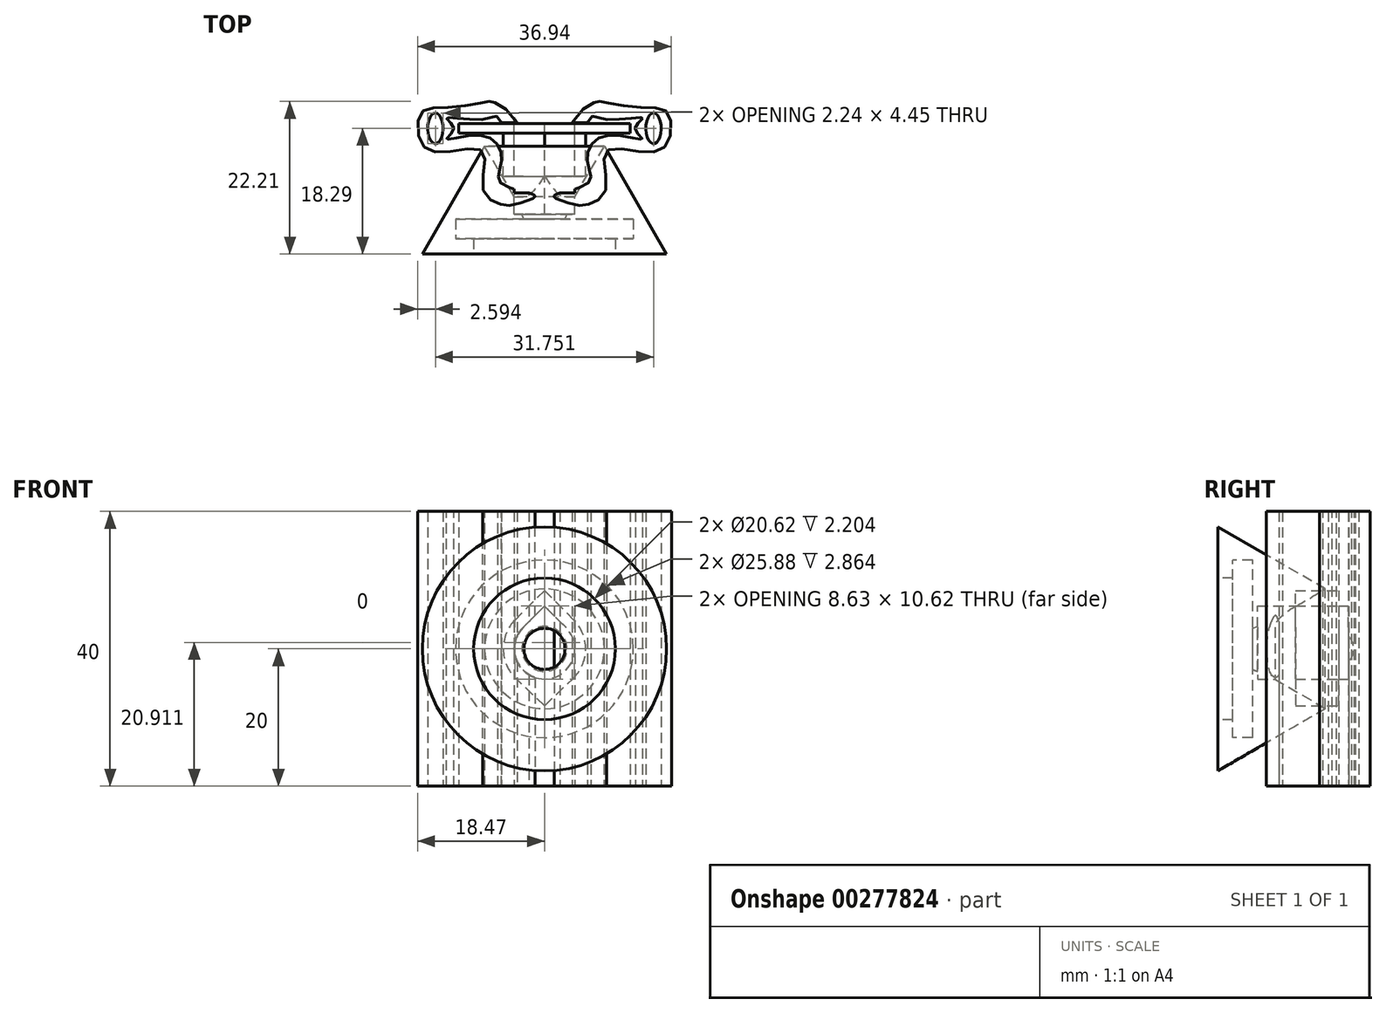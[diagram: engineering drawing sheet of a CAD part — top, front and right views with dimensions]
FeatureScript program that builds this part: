
annotation { "Feature Type Name" : "Feature", "Feature Type Description" : "" }
export const myFeature = defineFeature(function(context is Context, id is Id, definition is map)
    precondition{}
    {
        {
            var Q0;
            Q0=qCreatedBy(makeId("Top.planeOp"),FACE);
            cPlane(context, id + "F0", {"entities" : qUnion([Q0]), "cplaneType" : CPlaneType.OFFSET, "offset" : 20 * mm, "oppositeDirection" : true, "width" : 150 * mm, "height" : 150 * mm});
        }
        {
            var Q0;
            Q0=qCreatedBy(id+"F0.planeOp",FACE);
            var sketch = newSketch(context, id + "F1", { "sketchPlane" : qUnion([Q0])});
            skLineSegment(sketch, "E0.bottom", {"start": v(-12.5, 0.7) * mm, "end": v(12.5, 0.7) * mm});
            skLineSegment(sketch, "E0.top", {"start": v(-12.5, -0.7) * mm, "end": v(12.5, -0.7) * mm});
            skLineSegment(sketch, "E0.left", {"start": v(-12.5, 0.7) * mm, "end": v(-12.5, -0.7) * mm});
            skLineSegment(sketch, "E1", {"start": v(0, -20) * mm, "end": v(0, 20) * mm, "construction": true});
            skPoint(sketch, "E2", {"position": v(-4, 0.8) * mm});
            skPoint(sketch, "E3", {"position": v(-7.64, 3.87) * mm});
            skPoint(sketch, "E4", {"position": v(-8.39, 3.87) * mm});
            skPoint(sketch, "E5", {"position": v(-14.26, 3.02) * mm});
            skPoint(sketch, "E6", {"position": v(-17.93, 2.3) * mm});
            skPoint(sketch, "E7", {"position": v(-17.93, -2.14) * mm});
            skPoint(sketch, "E8", {"position": v(-14.26, -3.43) * mm});
            skPoint(sketch, "E9", {"position": v(-8.94, -3.43) * mm});
            skPoint(sketch, "E10", {"position": v(-8.94, -8.85) * mm});
            skPoint(sketch, "E11", {"position": v(-6.52, -11.05) * mm});
            skPoint(sketch, "E12", {"position": v(-4.14, -11.05) * mm});
            skLineSegment(sketch, "E13", {"start": v(-4, 0.8) * mm, "end": v(-6.28, 0.8) * mm});
            skPoint(sketch, "E14", {"position": v(-8.39, 1.36) * mm});
            skPoint(sketch, "E15", {"position": v(-14.26, 1.48) * mm});
            skPoint(sketch, "E16", {"position": v(-13.2, 0) * mm});
            skPoint(sketch, "E17", {"position": v(-14.26, -1.57) * mm});
            skPoint(sketch, "E18", {"position": v(-8.94, -1.07) * mm});
            skPoint(sketch, "E19", {"position": v(-6.24, -4.6) * mm});
            skPoint(sketch, "E20", {"position": v(-6.39, -7.96) * mm});
            skPoint(sketch, "E21", {"position": v(-1.4, -9.82) * mm});
            skFitSpline(sketch, "E22", {"points": [v(-6.28, 0.8) * mm, v(-8.39, 1.36) * mm, v(-14.26, 1.48) * mm, v(-13.2, 0) * mm, v(-14.26, -1.57) * mm, v(-8.94, -1.07) * mm, v(-6.24, -4.6) * mm, v(-6.39, -7.96) * mm, v(-1.4, -9.82) * mm, v(-4.14, -11.05) * mm, v(-6.52, -11.05) * mm, v(-8.94, -8.85) * mm, v(-8.94, -3.43) * mm, v(-14.26, -3.43) * mm, v(-17.93, -2.14) * mm, v(-17.93, 2.3) * mm, v(-14.26, 3.02) * mm, v(-8.39, 3.87) * mm, v(-7.64, 3.87) * mm, v(-4, 0.8) * mm], "startDerivative": vector(-46.48, 116.75) * mm, "endDerivative": vector(59.14, -105.88) * mm});
            skEllipse(sketch, "E23", {"center": v(-15.88, 0) * mm, "majorRadius": 2.23 * mm, "minorRadius": 1.12 * mm, "majorAxis": v(0, 1)});
            skLineSegment(sketch, "E24.top", {"start": v(0, -10.21) * mm, "end": v(-1.68, -10.21) * mm});
            skLineSegment(sketch, "E24.right", {"start": v(-5.2, -0.7) * mm, "end": v(-5.2, -8.6) * mm});
            skLineSegment(sketch, "E25.0", {"start": v(0, -9.41) * mm, "end": v(-4.4, -9.41) * mm});
            skLineSegment(sketch, "E25.2", {"start": v(0, -1.5) * mm, "end": v(-4.4, -1.5) * mm});
            skLineSegment(sketch, "E25.3", {"start": v(-4.4, -1.5) * mm, "end": v(-4.4, -9.41) * mm});
            skFitSpline(sketch, "E26.trimOffspring", {"points": [v(-6.28, 0.8) * mm, v(-8.39, 1.36) * mm, v(-14.26, 1.48) * mm, v(-13.2, 0) * mm, v(-14.26, -1.57) * mm, v(-8.94, -1.07) * mm, v(-6.24, -4.6) * mm, v(-6.39, -7.96) * mm, v(-1.4, -9.82) * mm, v(-4.14, -11.05) * mm, v(-6.52, -11.05) * mm, v(-8.94, -8.85) * mm, v(-8.94, -3.43) * mm, v(-14.26, -3.43) * mm, v(-17.93, -2.14) * mm, v(-17.93, 2.3) * mm, v(-14.26, 3.02) * mm, v(-8.39, 3.87) * mm, v(-7.64, 3.87) * mm, v(-4, 0.8) * mm], "startDerivative": vector(-46.48, 116.75) * mm, "endDerivative": vector(59.14, -105.88) * mm});
            skLineSegment(sketch, "E27", {"start": v(0, -1.5) * mm, "end": v(0, -0.7) * mm});
            skLineSegment(sketch, "E28", {"start": v(0, -10.21) * mm, "end": v(0, -9.41) * mm});
            skLineSegment(sketch, "E29.MirrorCS", {"start": v(12.5, 0.7) * mm, "end": v(12.5, -0.7) * mm});
            skSolve(sketch);
        }
        {
            var Q0;
            Q0=makeQuery(id+"F1.imprint","IMPRINT",FACE,{"disambiguationData":[TD([[makeQuery(id+"F1.imprint","IMPRINT",EDGE,{"derivedFrom":sQuery(id+"F1.wireOp",EDGE,"E13")}),-1.0]])]});
            extrude(context, id + "F2", {"entities" : qUnion([Q0]), "depth" : 40 * mm});
        }
        {
            var Q0;
            Q0=makeQuery(id+"F2.opExtrude","SWEPT_BODY",BODY,{"disambiguationData":[OSD([sQuery(id+"F1.wireOp",EDGE,"E0.top"),sQuery(id+"F1.wireOp",EDGE,"E13"),sQuery(id+"F1.wireOp",EDGE,"E22"),sQuery(id+"F1.wireOp",EDGE,"E23"),sQuery(id+"F1.wireOp",EDGE,"E24.top"),sQuery(id+"F1.wireOp",EDGE,"E24.right"),sQuery(id+"F1.wireOp",EDGE,"E25.0"),sQuery(id+"F1.wireOp",EDGE,"E25.2"),sQuery(id+"F1.wireOp",EDGE,"E25.3"),sQuery(id+"F1.wireOp",EDGE,"E26.trimOffspring"),sQuery(id+"F1.wireOp",EDGE,"E27"),sQuery(id+"F1.wireOp",EDGE,"E28")])]});
            var Q1;
            Q1=qCreatedBy(makeId("Right.planeOp"),FACE);
            mirror(context, id + "F3", {"operationType" : NewBodyOperationType.ADD, "entities" : qUnion([Q0]), "mirrorPlane" : qUnion([Q1])});
        }
        {
            var Q0;
            Q0=qCreatedBy(makeId("Front.planeOp"),FACE);
            var sketch = newSketch(context, id + "F4", { "sketchPlane" : qUnion([Q0])});
            skArc(sketch, "E30", {"start": v(0, -4.4) * mm, "mid": v(4.07, -1.68) * mm, "end": v(3.11, 3.11) * mm});
            skArc(sketch, "E31", {"start": v(4.13, -4.36) * mm, "mid": v(6, -0.08) * mm, "end": v(4.24, 4.24) * mm});
            skLineSegment(sketch, "E32", {"start": v(0, 0) * mm, "end": v(0, -20) * mm, "construction": true});
            skLineSegment(sketch, "E33", {"start": v(4.24, 4.24) * mm, "end": v(0, 8.49) * mm});
            skArc(sketch, "E34.MirrorC", {"start": v(4.24, 4.24) * mm, "mid": v(6, -0.08) * mm, "end": v(4.13, -4.36) * mm});
            skLineSegment(sketch, "E35", {"start": v(3.11, 3.11) * mm, "end": v(0, 6.22) * mm});
            skPoint(sketch, "E36", {"position": v(0, -4.4) * mm});
            skPoint(sketch, "E37", {"position": v(0, -6) * mm});
            skLineSegment(sketch, "E38", {"start": v(4.13, -4.36) * mm, "end": v(0, -8.26) * mm});
            skLineSegment(sketch, "E39", {"start": v(0, -8.26) * mm, "end": v(0, -4.4) * mm});
            skCircle(sketch, "E40", {"center": v(0, 0) * mm, "radius": 7.25 * mm, "construction": true});
            skLineSegment(sketch, "E41.bottom", {"start": v(-5.12, 5.13) * mm, "end": v(5.12, 5.13) * mm, "construction": true});
            skLineSegment(sketch, "E41.top", {"start": v(-5.12, -5.13) * mm, "end": v(5.12, -5.13) * mm, "construction": true});
            skLineSegment(sketch, "E41.left", {"start": v(-5.12, 5.13) * mm, "end": v(-5.12, -5.13) * mm, "construction": true});
            skLineSegment(sketch, "E41.right", {"start": v(5.12, 5.13) * mm, "end": v(5.12, -5.13) * mm, "construction": true});
            skLineSegment(sketch, "E42", {"start": v(0, 6.22) * mm, "end": v(0, 8.49) * mm});
            skLineSegment(sketch, "E43.MirrorCS", {"start": v(-3.11, 3.11) * mm, "end": v(0, 6.22) * mm});
            skLineSegment(sketch, "E44.MirrorCS", {"start": v(-4.24, 4.24) * mm, "end": v(0, 8.49) * mm});
            skArc(sketch, "E45.MirrorCS", {"start": v(-4.24, 4.24) * mm, "mid": v(-6, -0.08) * mm, "end": v(-4.13, -4.36) * mm});
            skLineSegment(sketch, "E46.MirrorCS", {"start": v(-4.13, -4.36) * mm, "end": v(0, -8.26) * mm});
            skPoint(sketch, "E47.MirrorCS.end.orphan", {"position": v(-3.11, 3.11) * mm});
            skArc(sketch, "E48.MirrorCS", {"start": v(0, -4.4) * mm, "mid": v(-4.07, -1.68) * mm, "end": v(-3.11, 3.11) * mm});
            skCircle(sketch, "E49", {"center": v(0, 0) * mm, "radius": 13.5 * mm});
            skSolve(sketch);
        }
        {
            var Q0;
            Q0=makeQuery(id+"F4.imprint","IMPRINT",FACE,{"disambiguationData":[TD([[makeQuery(id+"F4.imprint","IMPRINT",EDGE,{"derivedFrom":sQuery(id+"F4.wireOp",EDGE,"E30")}),-1.0]])]});
            var Q1;
            Q1=makeQuery(id+"F4.imprint","IMPRINT",FACE,{"disambiguationData":[TD([[makeQuery(id+"F4.imprint","IMPRINT",EDGE,{"derivedFrom":sQuery(id+"F4.wireOp",EDGE,"E39")}),1.0]])]});
            extrude(context, id + "F5", {"entities" : qUnion([Q0, Q1]), "depth" : 7 * mm});
        }
        {
            var Q0;
            Q0=makeQuery(id+"F1.imprint","IMPRINT",FACE,{"disambiguationData":[TD([[makeQuery(id+"F1.imprint","IMPRINT",EDGE,{"derivedFrom":sQuery(id+"F1.wireOp",EDGE,"E0.bottom")}),-1.0]])]});
            extrude(context, id + "F6", {"entities" : qUnion([Q0]), "depth" : 40 * mm});
        }
        {
            var Q0;
            Q0=makeQuery(id+"F4.imprint","IMPRINT",FACE,{"disambiguationData":[TD([[makeQuery(id+"F4.imprint","IMPRINT",EDGE,{"derivedFrom":sQuery(id+"F4.wireOp",EDGE,"E30")}),1.0]])]});
            extrude(context, id + "F7", {"entities" : qUnion([Q0]), "depth" : 25 * mm, "symmetric" : true});
        }
        {
            var Q0;
            Q0=makeQuery(id+"F6.opExtrude","SWEPT_BODY",BODY,{"disambiguationData":[OSD([sQuery(id+"F1.wireOp",EDGE,"E0.bottom"),sQuery(id+"F1.wireOp",EDGE,"E0.top"),sQuery(id+"F1.wireOp",EDGE,"E0.left"),sQuery(id+"F1.wireOp",EDGE,"E29.MirrorCS")])]});
            var Q1;
            Q1=makeQuery(id+"F5.opExtrude","SWEPT_BODY",BODY,{"disambiguationData":[OSD([sQuery(id+"F4.wireOp",EDGE,"E30"),sQuery(id+"F4.wireOp",EDGE,"E33"),sQuery(id+"F4.wireOp",EDGE,"E34.MirrorC"),sQuery(id+"F4.wireOp",EDGE,"E35"),sQuery(id+"F4.wireOp",EDGE,"E38"),sQuery(id+"F4.wireOp",EDGE,"E43.MirrorCS"),sQuery(id+"F4.wireOp",EDGE,"E44.MirrorCS"),sQuery(id+"F4.wireOp",EDGE,"E45.MirrorCS"),sQuery(id+"F4.wireOp",EDGE,"E46.MirrorCS"),sQuery(id+"F4.wireOp",EDGE,"E48.MirrorCS")])]});
            var Q2;
            Q2=makeQuery(id+"F2.opExtrude","SWEPT_BODY",BODY,{"disambiguationData":[OSD([sQuery(id+"F1.wireOp",EDGE,"E0.top"),sQuery(id+"F1.wireOp",EDGE,"E13"),sQuery(id+"F1.wireOp",EDGE,"E22"),sQuery(id+"F1.wireOp",EDGE,"E23"),sQuery(id+"F1.wireOp",EDGE,"E24.top"),sQuery(id+"F1.wireOp",EDGE,"E24.right"),sQuery(id+"F1.wireOp",EDGE,"E25.0"),sQuery(id+"F1.wireOp",EDGE,"E25.2"),sQuery(id+"F1.wireOp",EDGE,"E25.3"),sQuery(id+"F1.wireOp",EDGE,"E26.trimOffspring"),sQuery(id+"F1.wireOp",EDGE,"E27"),sQuery(id+"F1.wireOp",EDGE,"E28")])]});
            booleanBodies(context, id + "F8", {"operationType" : BooleanOperationType.SUBTRACTION, "tools" : qUnion([Q0]), "targets" : qUnion([Q1, Q2]), "keepTools" : true});
        }
        {
            var Q0;
            Q0=qCreatedBy(makeId("Top.planeOp"),FACE);
            var sketch = newSketch(context, id + "F9", { "sketchPlane" : qUnion([Q0])});
            skLineSegment(sketch, "E50", {"start": v(0, 0) * mm, "end": v(0, -19.08) * mm, "construction": true});
            skLineSegment(sketch, "E51", {"start": v(0, 0) * mm, "end": v(0, 11.84) * mm, "construction": true});
            skLineSegment(sketch, "E52", {"start": v(0, 0) * mm, "end": v(-7.21, 0) * mm});
            skLineSegment(sketch, "E53", {"start": v(-8.72, -2.62) * mm, "end": v(-17.77, -18.29) * mm});
            skLineSegment(sketch, "E54", {"start": v(-17.77, -18.29) * mm, "end": v(0, -18.29) * mm, "construction": true});
            skLineSegment(sketch, "E55", {"start": v(0, -18.29) * mm, "end": v(0, 0) * mm});
            skLineSegment(sketch, "E56", {"start": v(-17.77, -18.29) * mm, "end": v(-10.3, -18.29) * mm});
            skLineSegment(sketch, "E57", {"start": v(-10.3, -18.29) * mm, "end": v(-10.3, -16.08) * mm});
            skLineSegment(sketch, "E58", {"start": v(-10.3, -16.08) * mm, "end": v(-12.94, -16.08) * mm});
            skLineSegment(sketch, "E59", {"start": v(-12.94, -16.08) * mm, "end": v(-12.94, -13.22) * mm});
            skLineSegment(sketch, "E60", {"start": v(-12.94, -13.22) * mm, "end": v(-3, -13.22) * mm});
            skLineSegment(sketch, "E61", {"start": v(-3, -13.22) * mm, "end": v(-4.04, -10.57) * mm});
            skLineSegment(sketch, "E62", {"start": v(-4.04, -10.57) * mm, "end": v(-8.72, -2.62) * mm});
            skSolve(sketch);
        }
        {
            var Q0;
            Q0=makeQuery(id+"F9.imprint","IMPRINT",FACE,{"disambiguationData":[TD([[makeQuery(id+"F9.imprint","IMPRINT",EDGE,{"derivedFrom":sQuery(id+"F9.wireOp",EDGE,"E53")}),1.0]])]});
            var Q1;
            Q1=sQuery(id+"F9.wireOp",EDGE,"E51");
            revolve(context, id + "F10", {"entities" : qUnion([Q0]), "axis" : qUnion([Q1]), "revolveType" : RevolveType.FULL});
        }
        {
            var Q0;
            Q0=makeQuery(id+"F9.imprint","IMPRINT",FACE,{"disambiguationData":[TD([[makeQuery(id+"F9.imprint","IMPRINT",EDGE,{"derivedFrom":sQuery(id+"F9.wireOp",EDGE,"E53")}),1.0]])]});
            var Q1;
            Q1=sQuery(id+"F9.wireOp",EDGE,"E51");
            revolve(context, id + "F11", {"entities" : qUnion([Q0]), "axis" : qUnion([Q1]), "revolveType" : RevolveType.FULL});
        }
        {
            var Q0;
            Q0=makeQuery(id+"F7.opExtrude","SWEPT_BODY",BODY,{"disambiguationData":[OSD([sQuery(id+"F4.wireOp",EDGE,"E30"),sQuery(id+"F4.wireOp",EDGE,"E35"),sQuery(id+"F4.wireOp",EDGE,"E43.MirrorCS"),sQuery(id+"F4.wireOp",EDGE,"E48.MirrorCS")])]});
            var Q1;
            Q1=makeQuery(id+"F2.opExtrude","SWEPT_BODY",BODY,{"disambiguationData":[OSD([sQuery(id+"F1.wireOp",EDGE,"E0.top"),sQuery(id+"F1.wireOp",EDGE,"E13"),sQuery(id+"F1.wireOp",EDGE,"E22"),sQuery(id+"F1.wireOp",EDGE,"E23"),sQuery(id+"F1.wireOp",EDGE,"E24.top"),sQuery(id+"F1.wireOp",EDGE,"E24.right"),sQuery(id+"F1.wireOp",EDGE,"E25.0"),sQuery(id+"F1.wireOp",EDGE,"E25.2"),sQuery(id+"F1.wireOp",EDGE,"E25.3"),sQuery(id+"F1.wireOp",EDGE,"E26.trimOffspring"),sQuery(id+"F1.wireOp",EDGE,"E27"),sQuery(id+"F1.wireOp",EDGE,"E28")])]});
            var Q2;
            Q2=makeQuery(id+"F10.opRevolve","SWEPT_BODY",BODY,{"disambiguationData":[OSD([sQuery(id+"F9.wireOp",EDGE,"E53"),sQuery(id+"F9.wireOp",EDGE,"E56"),sQuery(id+"F9.wireOp",EDGE,"E57"),sQuery(id+"F9.wireOp",EDGE,"E58"),sQuery(id+"F9.wireOp",EDGE,"E59"),sQuery(id+"F9.wireOp",EDGE,"E60"),sQuery(id+"F9.wireOp",EDGE,"E61"),sQuery(id+"F9.wireOp",EDGE,"E62"),sQuery(id+"F9.wireOp",EDGE,"ARBjOSBC-HPB2-UAkz-hUhG-Eu1AZX3ne5Lv")])]});
            var Q3;
            Q3=makeQuery(id+"F6.opExtrude","SWEPT_BODY",BODY,{"disambiguationData":[OSD([sQuery(id+"F1.wireOp",EDGE,"E0.bottom"),sQuery(id+"F1.wireOp",EDGE,"E0.top"),sQuery(id+"F1.wireOp",EDGE,"E0.left"),sQuery(id+"F1.wireOp",EDGE,"E29.MirrorCS")])]});
            var Q4;
            Q4=makeQuery(id+"F5.opExtrude","SWEPT_BODY",BODY,{"disambiguationData":[OSD([sQuery(id+"F4.wireOp",EDGE,"E30"),sQuery(id+"F4.wireOp",EDGE,"E33"),sQuery(id+"F4.wireOp",EDGE,"E34.MirrorC"),sQuery(id+"F4.wireOp",EDGE,"E35"),sQuery(id+"F4.wireOp",EDGE,"E38"),sQuery(id+"F4.wireOp",EDGE,"E43.MirrorCS"),sQuery(id+"F4.wireOp",EDGE,"E44.MirrorCS"),sQuery(id+"F4.wireOp",EDGE,"E45.MirrorCS"),sQuery(id+"F4.wireOp",EDGE,"E46.MirrorCS"),sQuery(id+"F4.wireOp",EDGE,"E48.MirrorCS")])]});
            var Q5;
            Q5=makeQuery(id+"F11.opRevolve","SWEPT_BODY",BODY,{"disambiguationData":[OSD([sQuery(id+"F9.wireOp",EDGE,"E53"),sQuery(id+"F9.wireOp",EDGE,"E56"),sQuery(id+"F9.wireOp",EDGE,"E57"),sQuery(id+"F9.wireOp",EDGE,"E58"),sQuery(id+"F9.wireOp",EDGE,"E59"),sQuery(id+"F9.wireOp",EDGE,"E60"),sQuery(id+"F9.wireOp",EDGE,"E61"),sQuery(id+"F9.wireOp",EDGE,"E62"),sQuery(id+"F9.wireOp",EDGE,"ARBjOSBC-HPB2-UAkz-hUhG-Eu1AZX3ne5Lv")])]});
            booleanBodies(context, id + "F12", {"operationType" : BooleanOperationType.SUBTRACTION, "tools" : qUnion([Q0]), "targets" : qUnion([Q1, Q2, Q3, Q4, Q5])});
        }
    });
